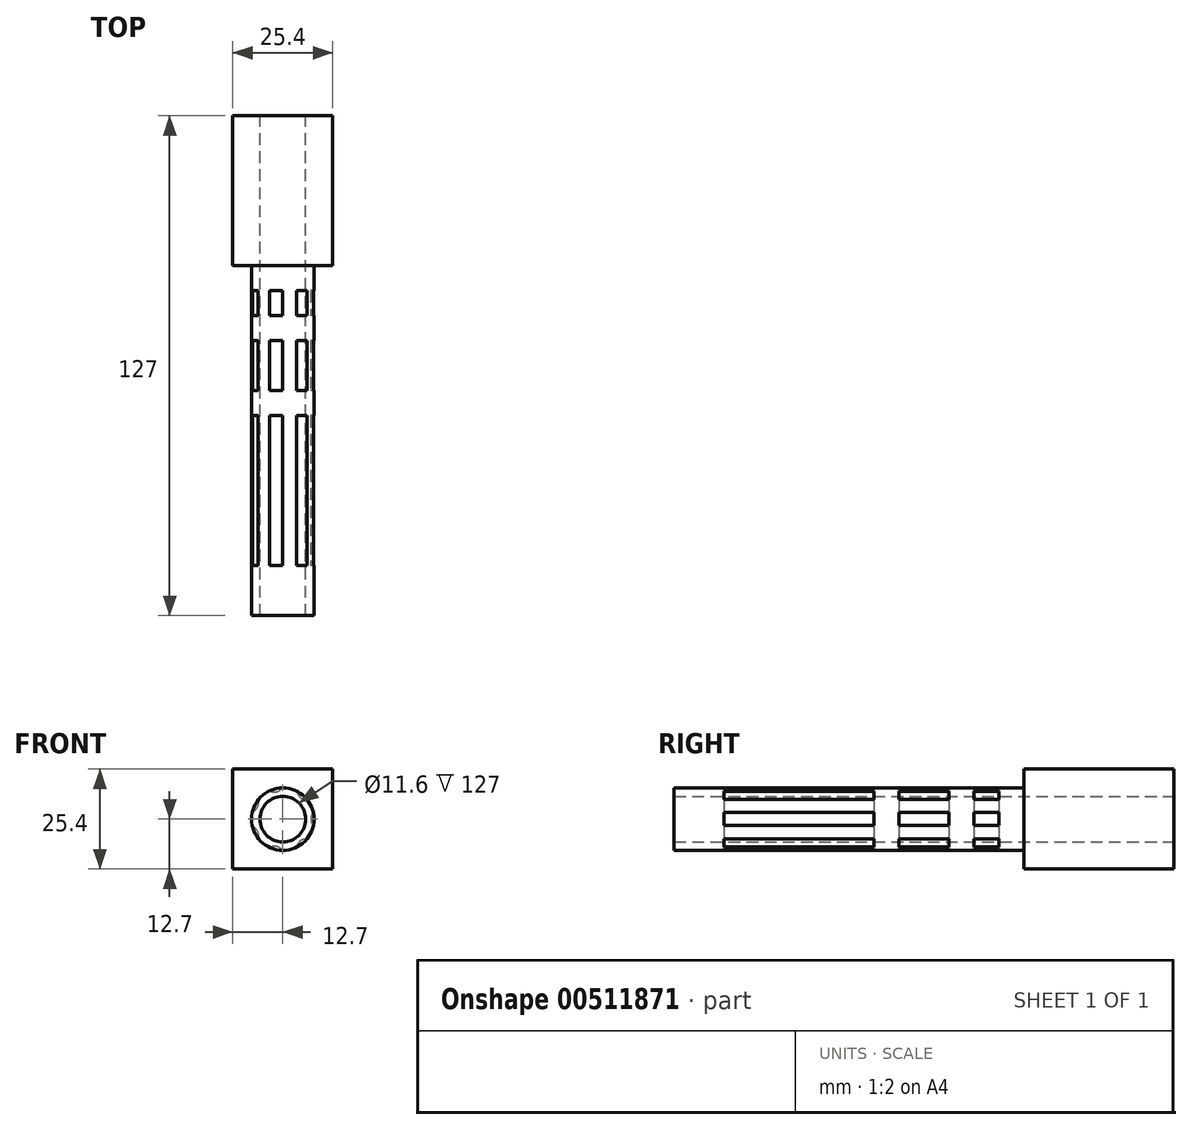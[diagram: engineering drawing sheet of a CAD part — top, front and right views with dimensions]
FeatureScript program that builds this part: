
annotation { "Feature Type Name" : "Feature", "Feature Type Description" : "" }
export const myFeature = defineFeature(function(context is Context, id is Id, definition is map)
    precondition{}
    {
        {
            var Q0;
            Q0=qCreatedBy(makeId("Front.planeOp"),FACE);
            var sketch = newSketch(context, id + "F0", { "sketchPlane" : qUnion([Q0])});
            skLineSegment(sketch, "E0.bottom", {"start": v(12.7, -12.7) * mm, "end": v(-12.7, -12.7) * mm});
            skLineSegment(sketch, "E0.top", {"start": v(12.7, 12.7) * mm, "end": v(-12.7, 12.7) * mm});
            skLineSegment(sketch, "E0.left", {"start": v(12.7, -12.7) * mm, "end": v(12.7, 12.7) * mm});
            skLineSegment(sketch, "E0.right", {"start": v(-12.7, -12.7) * mm, "end": v(-12.7, 12.7) * mm});
            skPoint(sketch, "E0.middle", {"position": v(0, 0) * mm});
            skCircle(sketch, "E1", {"center": v(0, 0) * mm, "radius": 7.94 * mm});
            skCircle(sketch, "E2", {"center": v(0, 0) * mm, "radius": 5.8 * mm});
            skSolve(sketch);
        }
        {
            var Q0;
            Q0=qSketchRegion(id+"F0",true);
            var Q1;
            Q1=makeQuery(id+"F0.imprint","IMPRINT",FACE,{"disambiguationData":[TD([[makeQuery(id+"F0.imprint","IMPRINT",EDGE,{"derivedFrom":sQuery(id+"F0.wireOp",EDGE,"E1")}),1.0]])]});
            extrude(context, id + "F1", {"entities" : qUnion([Q0, Q1]), "depth" : 38.1 * mm});
        }
        {
            var Q0;
            Q0=makeQuery(id+"F0.imprint","IMPRINT",FACE,{"disambiguationData":[TD([[makeQuery(id+"F0.imprint","IMPRINT",EDGE,{"derivedFrom":sQuery(id+"F0.wireOp",EDGE,"E1")}),1.0]])]});
            extrude(context, id + "F2", {"entities" : qUnion([Q0]), "operationType" : NewBodyOperationType.ADD, "depth" : 127 * mm, "offsetDistance" : 25.4 * mm});
        }
        {
            var Q0;
            Q0=makeQuery(id+"F2.opExtrude","CAP_FACE",FACE,{"disambiguationData":[OSD([sQuery(id+"F0.wireOp",EDGE,"E1")])],"isStart":false});
            var sketch = newSketch(context, id + "F3", { "sketchPlane" : qUnion([Q0])});
            skCircle(sketch, "E3", {"center": v(9.58, 0) * mm, "radius": 2.46 * mm});
            skCircle(sketch, "E4.1.0", {"center": v(5.97, 7.49) * mm, "radius": 2.46 * mm});
            skCircle(sketch, "E4.2.0", {"center": v(-2.13, 9.34) * mm, "radius": 2.46 * mm});
            skCircle(sketch, "E4.3.0", {"center": v(-8.63, 4.16) * mm, "radius": 2.46 * mm});
            skCircle(sketch, "E4.4.0", {"center": v(-8.63, -4.16) * mm, "radius": 2.46 * mm});
            skCircle(sketch, "E4.5.0", {"center": v(-2.13, -9.34) * mm, "radius": 2.46 * mm});
            skCircle(sketch, "E4.6.0", {"center": v(5.97, -7.49) * mm, "radius": 2.46 * mm});
            skPoint(sketch, "E4.center", {"position": v(0, 0) * mm});
            skSolve(sketch);
        }
        {
            var Q0;
            Q0=qSketchRegion(id+"F3",true);
            extrude(context, id + "F4", {"entities" : qUnion([Q0]), "operationType" : NewBodyOperationType.REMOVE, "oppositeDirection" : true, "depth" : 50.8 * mm, "offsetDistance" : 25.4 * mm, "hasSecondDirection" : true, "secondDirectionOppositeDirection" : true, "secondDirectionDepth" : 12.7 * mm});
        }
        {
            var Q0;
            Q0 = qSketchRegion(id + "F3", true);
            extrude(context, id + "F5", {"entities" : qUnion([Q0]), "operationType" : NewBodyOperationType.REMOVE, "oppositeDirection" : true, "depth" : 69.85 * mm, "offsetDistance" : 25.4 * mm, "hasSecondDirection" : true, "secondDirectionOppositeDirection" : true, "secondDirectionDepth" : 57.15 * mm});
        }
        {
            var Q0;
            Q0 = qSketchRegion(id + "F3", true);
            extrude(context, id + "F6", {"entities" : qUnion([Q0]), "operationType" : NewBodyOperationType.REMOVE, "oppositeDirection" : true, "depth" : 82.55 * mm, "offsetDistance" : 25.4 * mm, "hasSecondDirection" : true, "secondDirectionOppositeDirection" : true, "secondDirectionDepth" : 76.2 * mm});
        }
    });
